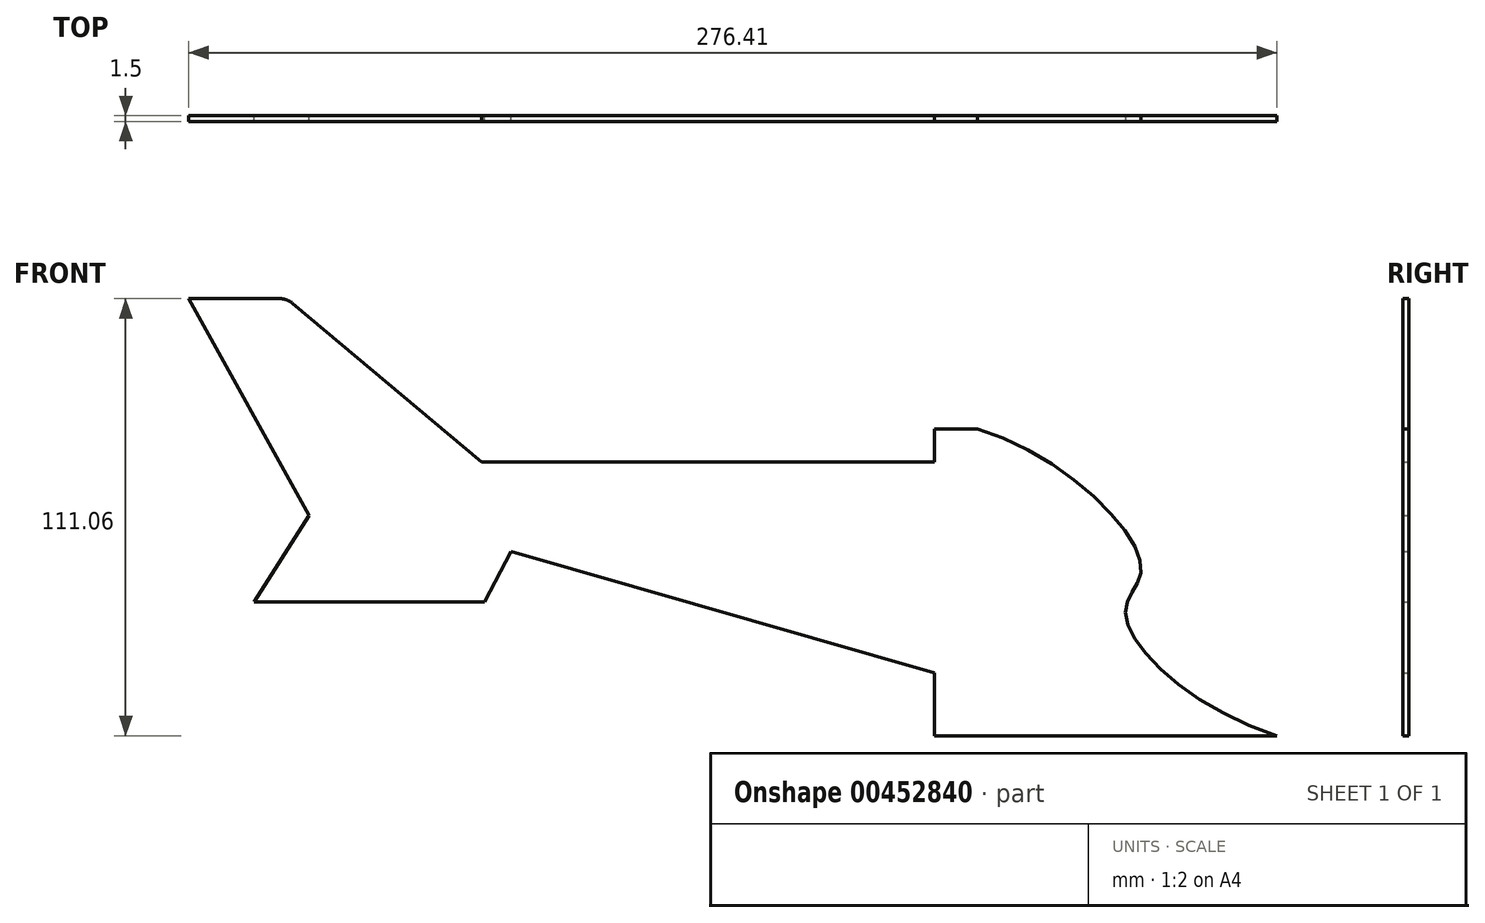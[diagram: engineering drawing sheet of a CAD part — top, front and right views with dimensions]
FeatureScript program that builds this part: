
annotation { "Feature Type Name" : "Feature", "Feature Type Description" : "" }
export const myFeature = defineFeature(function(context is Context, id is Id, definition is map)
    precondition{}
    {
        {
            var Q0;
            Q0=qCreatedBy(makeId("Front.planeOp"),FACE);
            var sketch = newSketch(context, id + "F0", { "sketchPlane" : qUnion([Q0])});
            skLineSegment(sketch, "E0", {"start": v(0, 62) * mm, "end": v(0, 53.6) * mm});
            skLineSegment(sketch, "E1", {"start": v(0, 53.6) * mm, "end": v(-115, 53.6) * mm});
            skLineSegment(sketch, "E2", {"start": v(0, 62) * mm, "end": v(11, 62) * mm});
            skLineSegment(sketch, "E3", {"start": v(0, 53.6) * mm, "end": v(0, -16) * mm});
            skLineSegment(sketch, "E4", {"start": v(0, -16) * mm, "end": v(87, -16) * mm});
            skLineSegment(sketch, "E5", {"start": v(0, -16) * mm, "end": v(0, 0) * mm});
            skLineSegment(sketch, "E6", {"start": v(0, 0) * mm, "end": v(-107.53, 30.83) * mm});
            skLineSegment(sketch, "E7", {"start": v(-107.53, 30.83) * mm, "end": v(-114.34, 18.03) * mm});
            skLineSegment(sketch, "E8", {"start": v(-114.34, 18.03) * mm, "end": v(-172.84, 18.03) * mm});
            skLineSegment(sketch, "E9", {"start": v(-172.84, 18.03) * mm, "end": v(-158.87, 39.96) * mm});
            skLineSegment(sketch, "E10", {"start": v(-158.87, 39.96) * mm, "end": v(-189.4, 95.06) * mm});
            skLineSegment(sketch, "E11", {"start": v(-189.4, 95.06) * mm, "end": v(-166.23, 95.06) * mm});
            skLineSegment(sketch, "E12", {"start": v(-163.02, 93.9) * mm, "end": v(-115, 53.6) * mm});
            skPoint(sketch, "E13.end.orphan", {"position": v(87, -16) * mm});
            skFitSpline(sketch, "E14", {"points": [v(11, 62) * mm, v(52.5, 27) * mm, v(48.5, 15.5) * mm, v(87, -16) * mm], "startDerivative": vector(149.53, -43.85) * mm, "endDerivative": vector(166.38, -53.46) * mm});
            skPoint(sketch, "E15.visualSharp", {"position": v(-164.4, 95.06) * mm});
            skArc(sketch, "E15.filletArc", {"start": v(-163.02, 93.9) * mm, "mid": v(-164.52, 94.76) * mm, "end": v(-166.23, 95.06) * mm});
            skSolve(sketch);
        }
        {
            var Q0;
            Q0 = qSketchRegion(id + "F0", true);
            extrude(context, id + "F1", {"entities" : qUnion([Q0]), "depth" : 1.5 * mm});
        }
    });
